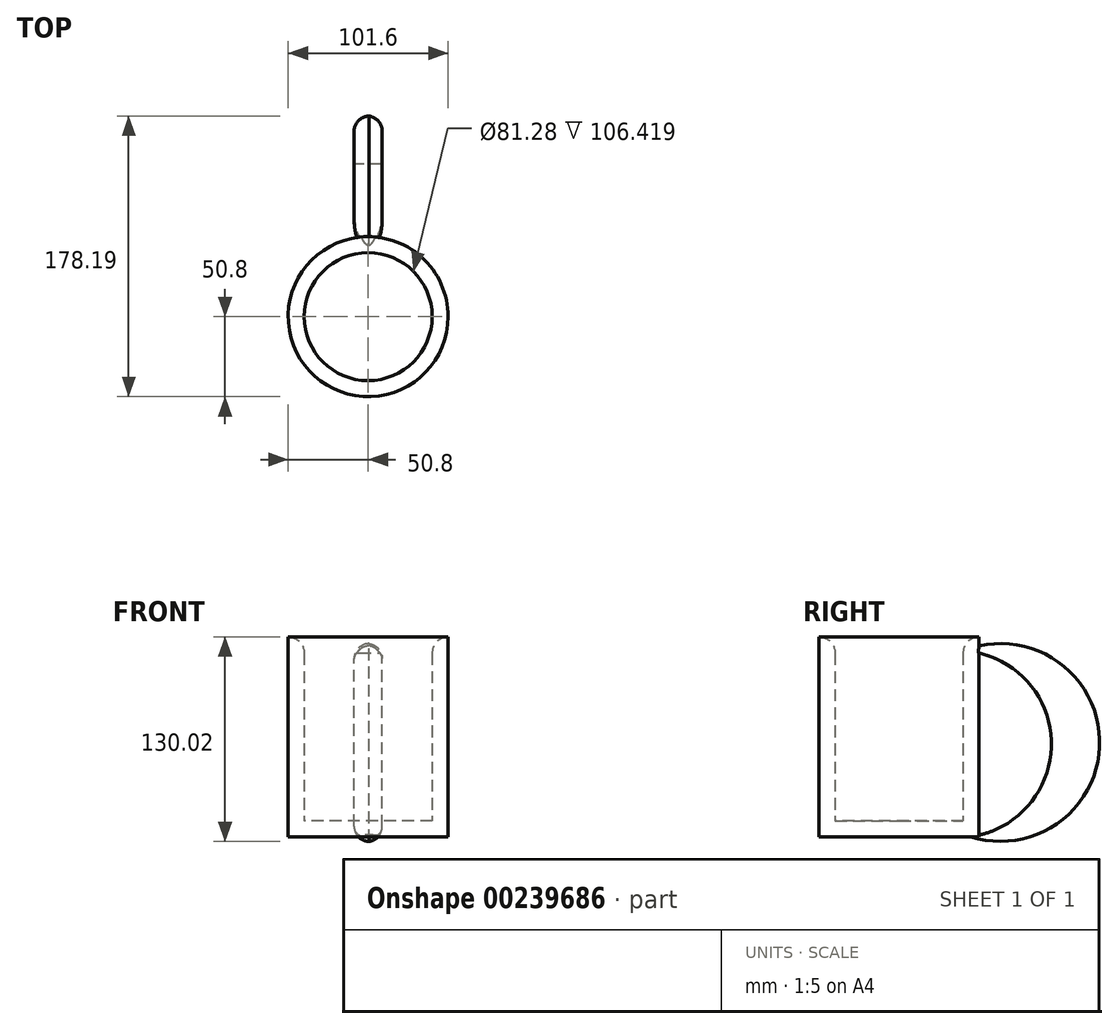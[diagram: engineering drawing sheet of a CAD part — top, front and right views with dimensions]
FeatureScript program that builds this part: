
annotation { "Feature Type Name" : "Feature", "Feature Type Description" : "" }
export const myFeature = defineFeature(function(context is Context, id is Id, definition is map)
    precondition{}
    {
        {
            var Q0;
            Q0=qCreatedBy(makeId("Top.planeOp"),FACE);
            var sketch = newSketch(context, id + "F0", { "sketchPlane" : qUnion([Q0])});
            skCircle(sketch, "E0", {"center": v(0, 0) * mm, "radius": 50.8 * mm});
            skSolve(sketch);
        }
        {
            var Q0;
            Q0 = qSketchRegion(id + "F0", true);
            extrude(context, id + "F1", {"entities" : qUnion([Q0]), "depth" : 127 * mm});
        }
        {
            var Q0;
            Q0=makeQuery(id+"F1.opExtrude","CAP_FACE",FACE,{"disambiguationData":[OSD([sQuery(id+"F0.wireOp",EDGE,"E0")])],"isStart":false});
            shell(context, id + "F2", {"entities" : qUnion([Q0]), "thickness" : 10.16 * mm});
        }
        {
            var Q0;
            {var subQ0=sQuery(id+"F0.wireOp",EDGE,"E0");Q0=makeQuery(id+"F2.opShell","OFFSET_EDGE",EDGE,{"disambiguationData":[OSD([subQ0]),TDD([makeQuery(id+"F1.opExtrude","CAP_EDGE",EDGE,{"disambiguationData":[OSD([subQ0])],"isStart":false})])]});}
            fillet(context, id + "F3", {"entities" : qUnion([Q0]), "radius" : 10.42 * mm, "tangentPropagation" : true, "allowEdgeOverflow" : false});
        }
        {
            var Q0;
            Q0=qCreatedBy(makeId("Right.planeOp"),FACE);
            var sketch = newSketch(context, id + "F4", { "sketchPlane" : qUnion([Q0])});
            skArc(sketch, "E1", {"start": v(45.33, 0) * mm, "mid": v(127.34, 62.16) * mm, "end": v(40.9, 118) * mm});
            skArc(sketch, "E2", {"start": v(45.33, 0) * mm, "mid": v(96.73, 61.01) * mm, "end": v(40.9, 118) * mm});
            skSolve(sketch);
        }
        {
            var Q0;
            Q0 = qSketchRegion(id + "F4", true);
            extrude(context, id + "F5", {"entities" : qUnion([Q0]), "operationType" : NewBodyOperationType.ADD, "endBound" : BoundingType.SYMMETRIC, "depth" : 17.78 * mm});
        }
        {
            var Q0;
            Q0=makeQuery(id+"F5.opExtrude","CAP_EDGE",EDGE,{"disambiguationData":[OSD([sQuery(id+"F4.wireOp",EDGE,"E1")])],"isStart":true});
            fillet(context, id + "F6", {"entities" : qUnion([Q0]), "radius" : 9.52 * mm, "tangentPropagation" : true, "allowEdgeOverflow" : false});
        }
        {
            var Q0;
            Q0=makeQuery(id+"F5.opExtrude","CAP_EDGE",EDGE,{"disambiguationData":[OSD([sQuery(id+"F4.wireOp",EDGE,"E1")])],"isStart":false});
            fillet(context, id + "F7", {"entities" : qUnion([Q0]), "radius" : 9.52 * mm, "tangentPropagation" : true, "allowEdgeOverflow" : false});
        }
    });
